# Revit family: FOCUS ROUND LIGHT
name_source: partatom
category: Lighting Fixtures
units: mm (PartAtom-declared; Revit-internal decimal feet)

## family parameters
Cut with Voids When Loaded = No
Host = Face
Light Source = Yes
Part Type = Normal
Room Calculation Point = No
Round Connector Dimension = Use Diameter
Shared = No

## types (10) — shared parameters
A = 0' - 1 3/16"
ANGLE = 75.00°
Acoustic = <By Category>
Air Craft Wire Length = 4' - 6 13/16"
Aircraft Cable Pendant Mount = No
Average life based on 77F(HRS) = 50000
B1 = 2' - 2 1/8"
B2 = 0' - 2 1/4"
CRI = 80
Color Filter = 16777215
Common Fixture = Yes
Default Elevation = 0' - 0"
Description = The Focus Round Light offers the FOCUS family of LED fixtures in diameters from 13.5 through 46.9. 
Recessed light source design achieving perfect glare control.
Dimming / Control = 0-10 V
Dimming Lamp Color Temperature Shift = <None>
Finish/Color = White-PMMA Aluminum
IP Rating = 20
Load Classification = Lighting
Manufacturer = Above All Lighting
Pendant Rod Length = 4' - 11"
Power Factor = 1
Rod Mounted = Yes
Surface Mount = No
Tilt Angle = -90.00°
Type Comments = FOCUS ROUND LIGHT
URL = https://www.abovealllighting.com
Voltage = 120-277 V

## per-type parameters (varying)
| type | Apparent Load | B | B3 | Fixture Diameter | Order number | Photometric Web File | Wattage Comments |
| FRD14-23-40801 | 29 VA | 0' - 4 21/32" | 0' - 3 5/32" | 0' - 6 29/32" | 16103 | FRD14-23-40801-4000K_IESNA2002.IES | 23 W |
| FRD18-42-40801 | 53 VA | 0' - 6 19/32" | 0' - 5 3/32" | 0' - 8 27/32" | 16104 | FRD18-42-40801-4000K_IESNA2002.IES | 42 W |
| FRD24-64-40801 | 80 VA | 0' - 9 9/16" | 0' - 8 1/16" | 0' - 11 13/16" | 16105 | FRD24-64-40801-4000K_IESNA2002.IES | 64 W |
| FRD35-102-40801 | 128 VA | 1' - 3 7/16" | 1' - 1 15/16" | 1' - 5 11/16" | 16106 | FRD35-102-40801-4000K_IESNA2002.IES | 102 W |
| FRD47-136-40801 | 170 VA | 1' - 9 11/32" | 1' - 7 27/32" | 1' - 11 19/32" | 16107 | FRD47-136-40801-4000K_IESNA2002.IES | 136 W |
| FRID14-28-40801 | 35 VA | 0' - 4 21/32" | 0' - 3 5/32" | 0' - 6 29/32" | 16108 | FRID14-28-40801-4000K_IESNA2002.IES | 28 W |
| FRID18-42-40801 | 53 VA | 0' - 6 19/32" | 0' - 5 3/32" | 0' - 8 27/32" | 16109 | FRID18-42-40801-4000K_IESNA2002.IES | 42 W |
| FRID24-64-40801 | 80 VA | 0' - 9 9/16" | 0' - 8 1/16" | 0' - 11 13/16" | 16110 | FRID24-64-40801-4000K_IESNA2002.IES | 64 W |
| FRID35-102-40801 | 128 VA | 1' - 3 7/16" | 1' - 1 15/16" | 1' - 5 11/16" | 16111 | FRID35-102-40801-4000K_IESNA2002.IES | 102 W |
| FRID47-136-40801 | 170 VA | 1' - 9 11/32" | 1' - 7 27/32" | 1' - 11 19/32" | 16112 | FRID47-136-40801-4000K_IESNA2002.IES | 136 W |

note: column(s) folded — value = type name in every type: Model

## geometry (parser evidence)
native form markers: Sweep x41
no freeform markers — native parametric forms only
